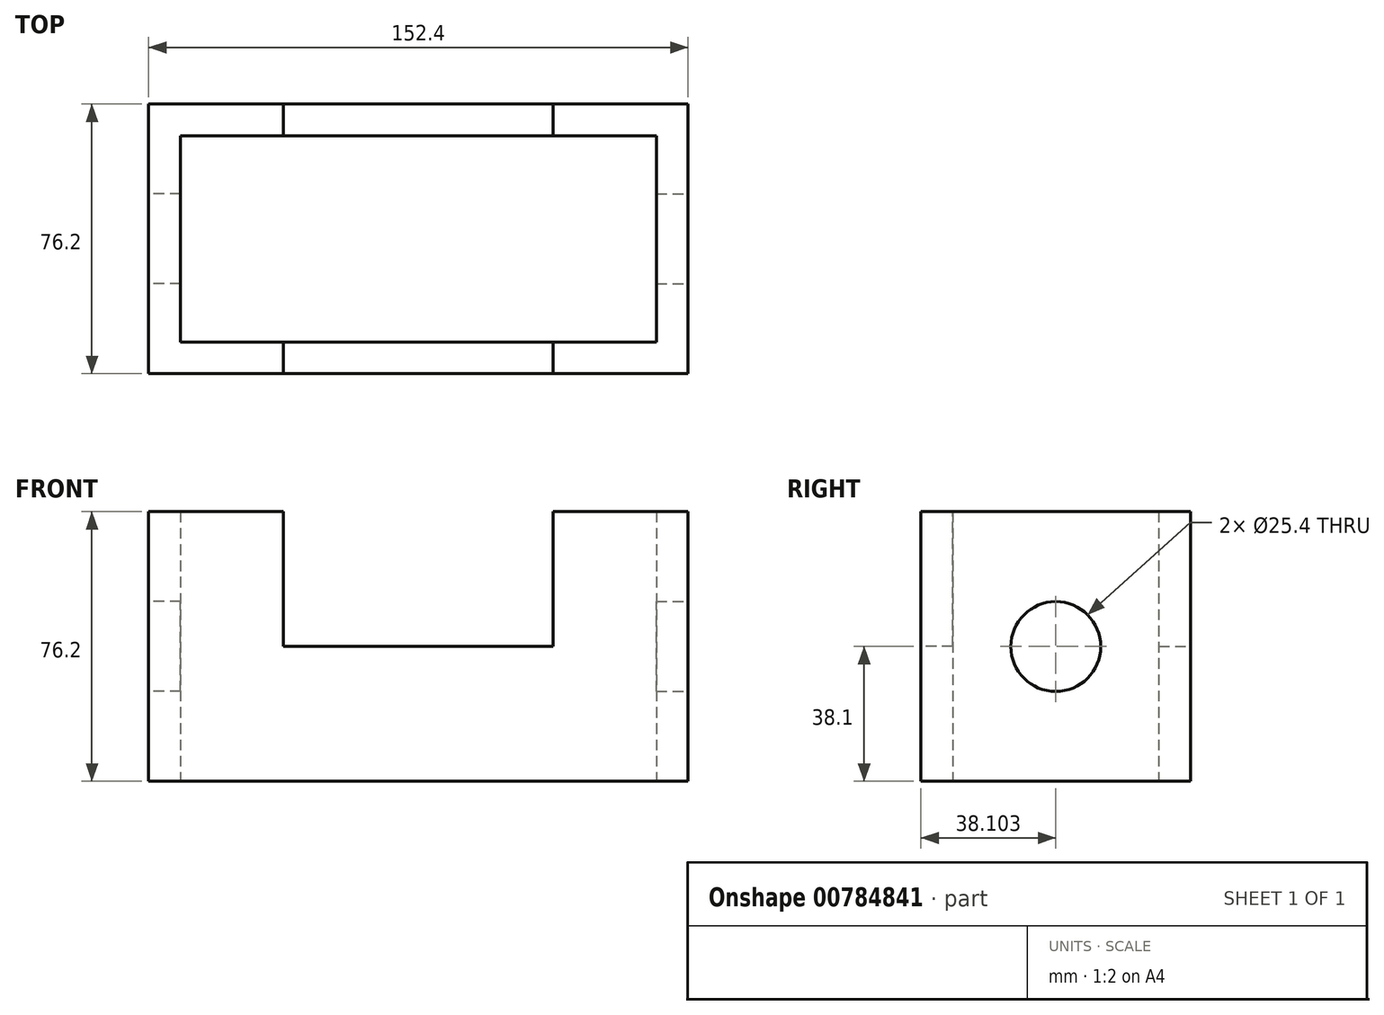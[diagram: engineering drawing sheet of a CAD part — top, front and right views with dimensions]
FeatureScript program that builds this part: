
annotation { "Feature Type Name" : "Feature", "Feature Type Description" : "" }
export const myFeature = defineFeature(function(context is Context, id is Id, definition is map)
    precondition{}
    {
        {
            var Q0;
            Q0=qCreatedBy(makeId("Top.planeOp"),FACE);
            var sketch = newSketch(context, id + "F0", { "sketchPlane" : qUnion([Q0])});
            skLineSegment(sketch, "E0.bottom", {"start": v(-79.71, 54.7) * mm, "end": v(72.69, 54.7) * mm});
            skLineSegment(sketch, "E0.top", {"start": v(-79.71, -21.5) * mm, "end": v(72.69, -21.5) * mm});
            skLineSegment(sketch, "E0.left", {"start": v(-79.71, 54.7) * mm, "end": v(-79.71, -21.5) * mm});
            skLineSegment(sketch, "E0.right", {"start": v(72.69, 54.7) * mm, "end": v(72.69, -21.5) * mm});
            skLineSegment(sketch, "E1.bottom", {"start": v(-70.73, 45.72) * mm, "end": v(63.7, 45.72) * mm});
            skLineSegment(sketch, "E1.top", {"start": v(-70.73, -12.52) * mm, "end": v(63.7, -12.52) * mm});
            skLineSegment(sketch, "E1.left", {"start": v(-70.73, 45.72) * mm, "end": v(-70.73, -12.52) * mm});
            skLineSegment(sketch, "E1.right", {"start": v(63.7, 45.72) * mm, "end": v(63.7, -12.52) * mm});
            skSolve(sketch);
        }
        {
            var Q0;
            Q0=makeQuery(id+"F0.imprint","IMPRINT",FACE,{"disambiguationData":[TD([[makeQuery(id+"F0.imprint","IMPRINT",EDGE,{"derivedFrom":sQuery(id+"F0.wireOp",EDGE,"E0.bottom")}),-1.0]])]});
            extrude(context, id + "F1", {"entities" : qUnion([Q0]), "depth" : 76.2 * mm, "offsetDistance" : 25.4 * mm});
        }
        {
            var Q0;
            Q0=makeQuery(id+"F1.opExtrude","SWEPT_FACE",FACE,{"disambiguationData":[OSD([sQuery(id+"F0.wireOp",EDGE,"E0.top")])]});
            var sketch = newSketch(context, id + "F2", { "sketchPlane" : qUnion([Q0])});
            skLineSegment(sketch, "E2", {"start": v(-79.71, 76.2) * mm, "end": v(-41.61, 76.2) * mm});
            skLineSegment(sketch, "E3", {"start": v(72.69, 76.2) * mm, "end": v(34.59, 76.2) * mm});
            skLineSegment(sketch, "E4", {"start": v(-41.61, 76.2) * mm, "end": v(-41.61, 38.1) * mm});
            skLineSegment(sketch, "E5", {"start": v(-41.61, 38.1) * mm, "end": v(34.59, 38.1) * mm});
            skLineSegment(sketch, "E6", {"start": v(34.59, 38.1) * mm, "end": v(34.59, 76.2) * mm});
            skSolve(sketch);
        }
        {
            var Q0;
            {var subQ0=sQuery(id+"F2.wireOp",EDGE,"E4");Q0=makeQuery(id+"F2.imprint","IMPRINT",FACE,{"disambiguationData":[TD([[makeQuery(id+"F2.imprint","IMPRINT",EDGE,{"derivedFrom":subQ0}),1.0]])]});}
            extrude(context, id + "F3", {"entities" : qUnion([Q0]), "operationType" : NewBodyOperationType.REMOVE, "oppositeDirection" : true, "depth" : 25.4 * mm, "offsetDistance" : 25.4 * mm});
        }
        {
            var Q0;
            Q0=makeQuery(id+"F1.opExtrude","SWEPT_FACE",FACE,{"disambiguationData":[OSD([sQuery(id+"F0.wireOp",EDGE,"E0.bottom")])]});
            var sketch = newSketch(context, id + "F4", { "sketchPlane" : qUnion([Q0])});
            skLineSegment(sketch, "E7", {"start": v(-72.69, 76.2) * mm, "end": v(-34.59, 76.2) * mm});
            skLineSegment(sketch, "E8", {"start": v(79.71, 76.2) * mm, "end": v(41.61, 76.2) * mm});
            skLineSegment(sketch, "E9", {"start": v(-34.59, 76.2) * mm, "end": v(-34.59, 38.1) * mm});
            skLineSegment(sketch, "E10", {"start": v(41.61, 76.2) * mm, "end": v(41.61, 38.1) * mm});
            skLineSegment(sketch, "E11", {"start": v(-34.59, 38.1) * mm, "end": v(41.61, 38.1) * mm});
            skSolve(sketch);
        }
        {
            var Q0;
            {var subQ0=sQuery(id+"F4.wireOp",EDGE,"E9");Q0=makeQuery(id+"F4.imprint","IMPRINT",FACE,{"disambiguationData":[TD([[makeQuery(id+"F4.imprint","IMPRINT",EDGE,{"derivedFrom":subQ0}),1.0]])]});}
            extrude(context, id + "F5", {"entities" : qUnion([Q0]), "operationType" : NewBodyOperationType.REMOVE, "oppositeDirection" : true, "depth" : 25.4 * mm, "offsetDistance" : 25.4 * mm});
        }
        {
            var Q0;
            Q0=makeQuery(id+"F1.opExtrude","SWEPT_FACE",FACE,{"disambiguationData":[OSD([sQuery(id+"F0.wireOp",EDGE,"E0.left")])]});
            var sketch = newSketch(context, id + "F6", { "sketchPlane" : qUnion([Q0])});
            skCircle(sketch, "E12", {"center": v(-16.6, 38.1) * mm, "radius": 12.7 * mm});
            skSolve(sketch);
        }
        {
            var Q0;
            Q0=makeQuery(id+"F6.imprint","IMPRINT",FACE,{"disambiguationData":[TD([[makeQuery(id+"F6.imprint","IMPRINT",EDGE,{"derivedFrom":sQuery(id+"F6.wireOp",EDGE,"E12")}),1.0]])]});
            extrude(context, id + "F7", {"entities" : qUnion([Q0]), "operationType" : NewBodyOperationType.REMOVE, "oppositeDirection" : true, "depth" : 51.56 * mm, "offsetDistance" : 25.4 * mm});
        }
        {
            var Q0;
            Q0=makeQuery(id+"F1.opExtrude","SWEPT_FACE",FACE,{"disambiguationData":[OSD([sQuery(id+"F0.wireOp",EDGE,"E0.right")])]});
            var sketch = newSketch(context, id + "F8", { "sketchPlane" : qUnion([Q0])});
            skCircle(sketch, "E13", {"center": v(16.6, 38.1) * mm, "radius": 12.7 * mm});
            skSolve(sketch);
        }
        {
            var Q0;
            Q0=makeQuery(id+"F8.imprint","IMPRINT",FACE,{"disambiguationData":[TD([[makeQuery(id+"F8.imprint","IMPRINT",EDGE,{"derivedFrom":sQuery(id+"F8.wireOp",EDGE,"E13")}),1.0]])]});
            extrude(context, id + "F9", {"entities" : qUnion([Q0]), "operationType" : NewBodyOperationType.REMOVE, "oppositeDirection" : true, "depth" : 25.4 * mm, "offsetDistance" : 25.4 * mm});
        }
    });
